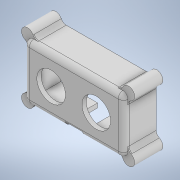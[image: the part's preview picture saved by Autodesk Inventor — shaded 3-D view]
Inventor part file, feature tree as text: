
AUTODESK INVENTOR PART (.ipt)
format: ipt  version: 2020 (Build 240168000, 168)  size: 386,560 bytes
history: native  units: in
note: dims shown in document units (in); Inventor stores cm internally (conversion verified against a paired STEP export)
features: extrude x7, sketch x6, fillet x2, plane x2, mirror x2, projected_geometry x2
ambient origin geometry x8: Origin, YZ Plane, XZ Plane, XY Plane, X Axis, Y Axis, Z Axis, Center Point
bodies: Solid1 (feature_tree)
feature tree (21):
  extrude  "Extrusion1"  Depth=0.66in
  sketch  "Sketch3"  dims[d2=0.38in d4=0.85in]
  extrude  "Extrusion2"  Depth=0.85in
  extrude  "Extrusion3"  Depth=0.41in
  fillet  "Fillet1"  Radius=0.41in
  extrude  "Extrusion4"  Depth=0.1in
  extrude  "Extrusion5"  Depth=0.65in TaperAngle=0.0deg
  extrude  "Extrusion6"  Depth=0.125in
  extrude  "Extrusion7"  Depth=0.125in
  plane  "Work Plane1"
  plane  "Work Plane2"
  mirror  "Mirror1"
  mirror  "Mirror2"
  fillet  "Fillet2"  Radius=1.09in
  sketch  "Sketch2"  dims[d0=0.66in d1=0.66in]
  projected_geometry  "Projected Loop1"
  sketch  "Sketch4"  dims[d5=0.43in d6=0.41in d7=0.41in]
  sketch  "Sketch5"  dims[d8=0.1in d9=0.0in d11=0.1in]
  projected_geometry  "Projected Loop2"
  sketch  "Sketch6"  dims[d12=0.12in d13=0.65in d14=0.0in]
  sketch  "Sketch7"  dims[d15=1.25in d16=0.0in d17=0.125in d18=0.6in d19=1.09in d20=0.0in d21=0.597in d22=0.0in d23=0.1094in d24=0.14in d25=0.65in d26=0.0in d27=0.05in d28=0.0in d29=0.125in d30=0.4in]
